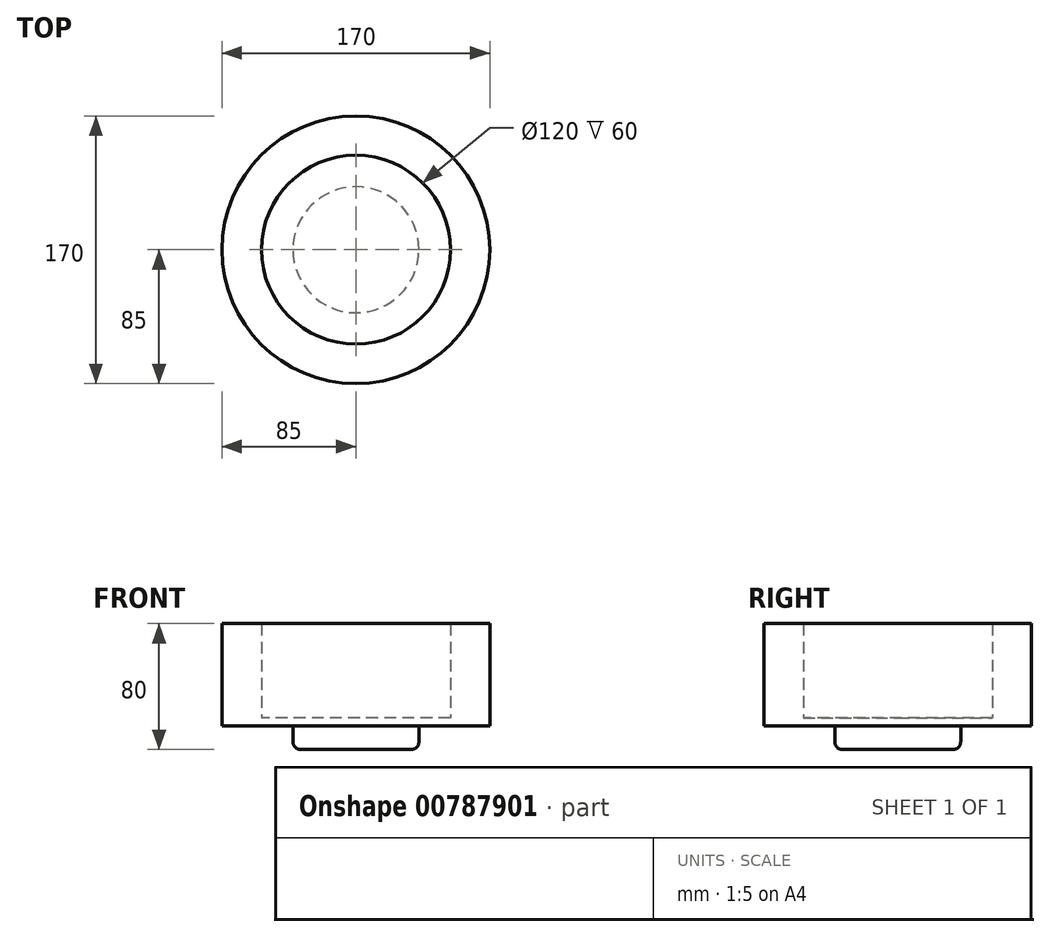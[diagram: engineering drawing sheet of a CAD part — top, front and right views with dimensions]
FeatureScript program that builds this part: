
annotation { "Feature Type Name" : "Feature", "Feature Type Description" : "" }
export const myFeature = defineFeature(function(context is Context, id is Id, definition is map)
    precondition{}
    {
        {
            var Q0;
            Q0=qCreatedBy(makeId("Top.planeOp"),FACE);
            var sketch = newSketch(context, id + "F0", { "sketchPlane" : qUnion([Q0])});
            skCircle(sketch, "E0", {"center": v(0, 0) * mm, "radius": 85 * mm});
            skCircle(sketch, "E1", {"center": v(0, 0) * mm, "radius": 60 * mm});
            skCircle(sketch, "E2", {"center": v(0, 0) * mm, "radius": 40 * mm});
            skSolve(sketch);
        }
        {
            var Q0;
            Q0=makeQuery(id+"F0.imprint","IMPRINT",FACE,{"disambiguationData":[TD([[makeQuery(id+"F0.imprint","IMPRINT",EDGE,{"derivedFrom":sQuery(id+"F0.wireOp",EDGE,"E0")}),1.0]])]});
            extrude(context, id + "F1", {"entities" : qUnion([Q0]), "depth" : 65 * mm, "offsetDistance" : 25 * mm});
        }
        {
            var Q0;
            Q0=makeQuery(id+"F0.imprint","IMPRINT",FACE,{"disambiguationData":[TD([[makeQuery(id+"F0.imprint","IMPRINT",EDGE,{"derivedFrom":sQuery(id+"F0.wireOp",EDGE,"E1")}),1.0]])]});
            extrude(context, id + "F2", {"entities" : qUnion([Q0]), "operationType" : NewBodyOperationType.ADD, "depth" : 5 * mm, "offsetDistance" : 25 * mm});
        }
        {
            var Q0;
            Q0=makeQuery(id+"F0.imprint","IMPRINT",FACE,{"disambiguationData":[TD([[makeQuery(id+"F0.imprint","IMPRINT",EDGE,{"derivedFrom":sQuery(id+"F0.wireOp",EDGE,"E2")}),1.0]])]});
            extrude(context, id + "F3", {"entities" : qUnion([Q0]), "operationType" : NewBodyOperationType.ADD, "depth" : 5 * mm, "offsetDistance" : 25 * mm, "hasSecondDirection" : true, "secondDirectionOppositeDirection" : true, "secondDirectionDepth" : 15 * mm});
        }
        {
            var Q0;
            Q0=makeQuery(id+"F3.opExtrude","CAP_EDGE",EDGE,{"disambiguationData":[OSD([sQuery(id+"F0.wireOp",EDGE,"E2")])],"isStart":true});
            fillet(context, id + "F4", {"entities" : qUnion([Q0]), "radius" : 5 * mm, "tangentPropagation" : true, "allowEdgeOverflow" : false});
        }
    });
